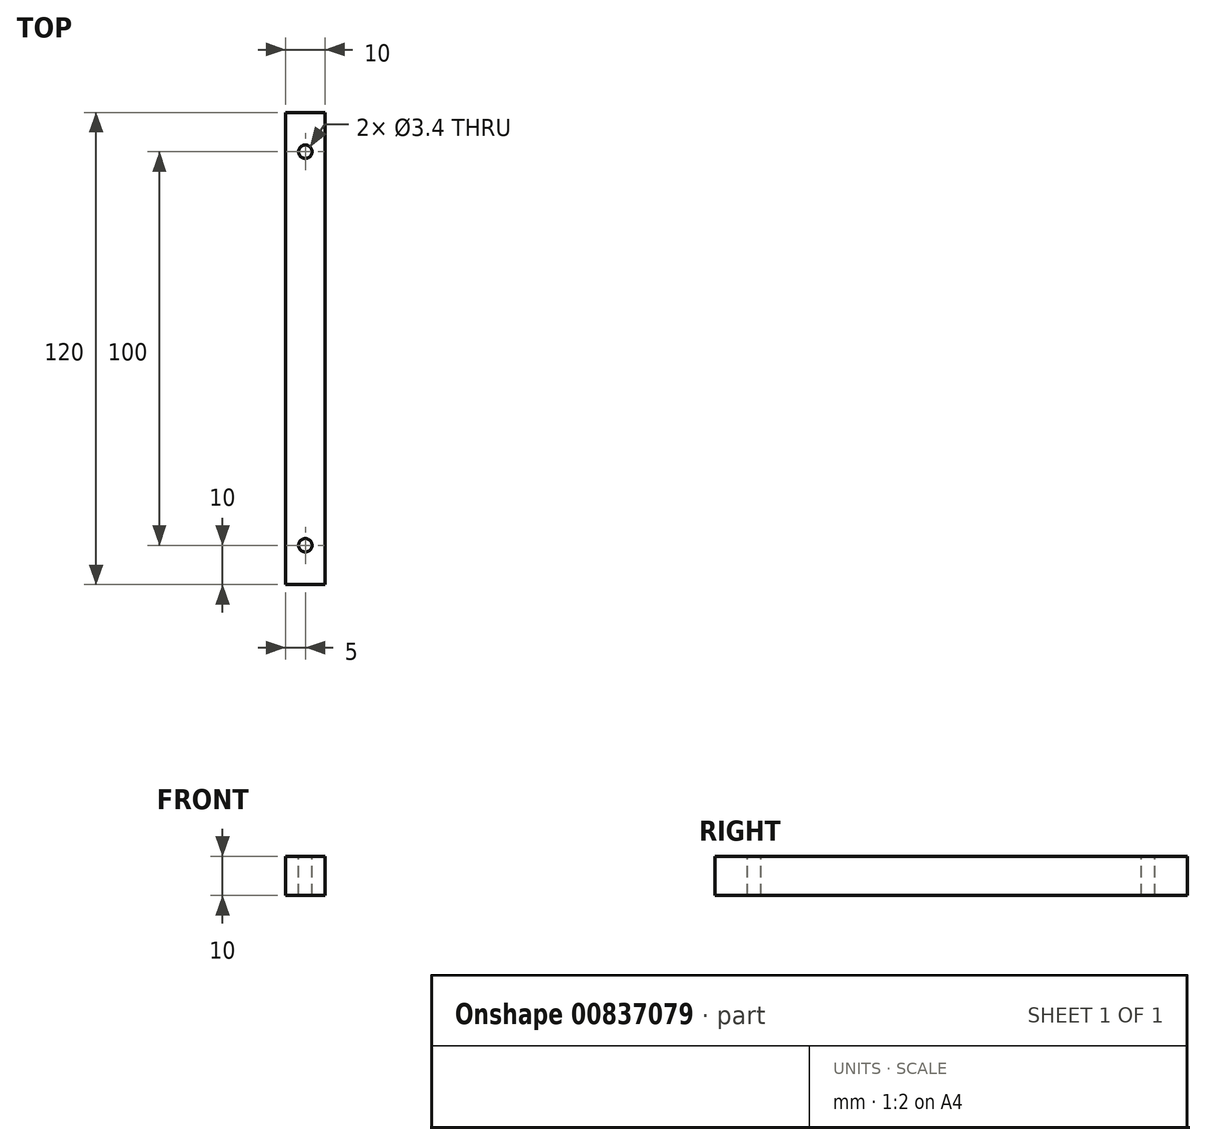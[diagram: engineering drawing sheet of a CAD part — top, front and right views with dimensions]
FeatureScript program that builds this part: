
annotation { "Feature Type Name" : "Feature", "Feature Type Description" : "" }
export const myFeature = defineFeature(function(context is Context, id is Id, definition is map)
    precondition{}
    {
        {
            var Q0;
            Q0=qCreatedBy(makeId("Front.planeOp"),FACE);
            var sketch = newSketch(context, id + "F0", { "sketchPlane" : qUnion([Q0])});
            skLineSegment(sketch, "E0.bottom", {"start": v(-5, 5) * mm, "end": v(5, 5) * mm});
            skLineSegment(sketch, "E0.top", {"start": v(-5, -5) * mm, "end": v(5, -5) * mm});
            skLineSegment(sketch, "E0.left", {"start": v(-5, 5) * mm, "end": v(-5, -5) * mm});
            skLineSegment(sketch, "E0.right", {"start": v(5, 5) * mm, "end": v(5, -5) * mm});
            skPoint(sketch, "E0.middle", {"position": v(0, 0) * mm});
            skSolve(sketch);
        }
        {
            var Q0;
            Q0=makeQuery(id+"F0.imprint","IMPRINT",FACE,{"disambiguationData":[TD([[makeQuery(id+"F0.imprint","IMPRINT",EDGE,{"derivedFrom":sQuery(id+"F0.wireOp",EDGE,"E0.bottom")}),-1.0]])]});
            extrude(context, id + "F1", {"entities" : qUnion([Q0]), "depth" : 120 * mm, "offsetDistance" : 25 * mm});
        }
        {
            var Q0;
            Q0=makeQuery(id+"F1.opExtrude","SWEPT_FACE",FACE,{"disambiguationData":[OSD([sQuery(id+"F0.wireOp",EDGE,"E0.bottom")])]});
            var sketch = newSketch(context, id + "F2", { "sketchPlane" : qUnion([Q0])});
            skLineSegment(sketch, "E1", {"start": v(0, -120) * mm, "end": v(0, 0) * mm, "construction": true});
            skLineSegment(sketch, "E2", {"start": v(0, -120) * mm, "end": v(-59.43, -120) * mm, "construction": true});
            skLineSegment(sketch, "E3", {"start": v(-58.52, -110) * mm, "end": v(26.37, -110) * mm, "construction": true});
            skLineSegment(sketch, "E4", {"start": v(-56.7, -10) * mm, "end": v(28.65, -10) * mm, "construction": true});
            skLineSegment(sketch, "E5", {"start": v(0, 0) * mm, "end": v(-55.78, 0) * mm, "construction": true});
            skPoint(sketch, "E6", {"position": v(0, -10) * mm});
            skPoint(sketch, "E7", {"position": v(0, -110) * mm});
            skSolve(sketch);
        }
        {
            var Q0;
            Q0=sQuery(id+"F2.wireOp",VERTEX,"E6");
            var Q1;
            Q1=sQuery(id+"F2.wireOp",VERTEX,"E7");
            var Q2;
            Q2=makeQuery(id+"F1.opExtrude","SWEPT_BODY",BODY,{"disambiguationData":[OSD([sQuery(id+"F0.wireOp",EDGE,"E0.bottom"),sQuery(id+"F0.wireOp",EDGE,"E0.top"),sQuery(id+"F0.wireOp",EDGE,"E0.left"),sQuery(id+"F0.wireOp",EDGE,"E0.right")])]});
            hole(context, id + "F3", {"style" : HoleStyle.SIMPLE, "endStyle" : HoleEndStyle.THROUGH, "standardTappedOrClearance" : lookupTablePath({ "fit" : "Normal", "standard" : "ISO", "size" : "M3", "type" : "Clearance" }), "standardBlindInLast" : lookupTablePath({ "fit" : "Normal", "standard" : "ISO", "engagement" : "75%", "pitch" : "0.5 mm", "size" : "M3", "type" : "Clearance & tapped" }), "holeDiameter" : 3.4 * mm, "majorDiameter" : 5 * mm, "isTappedThrough" : true, "tappedDepth" : 12 * mm, "tapClearance" : 3, "startFromSketch" : true, "locations" : qUnion([Q0, Q1]), "scope" : qUnion([Q2])});
        }
    });
